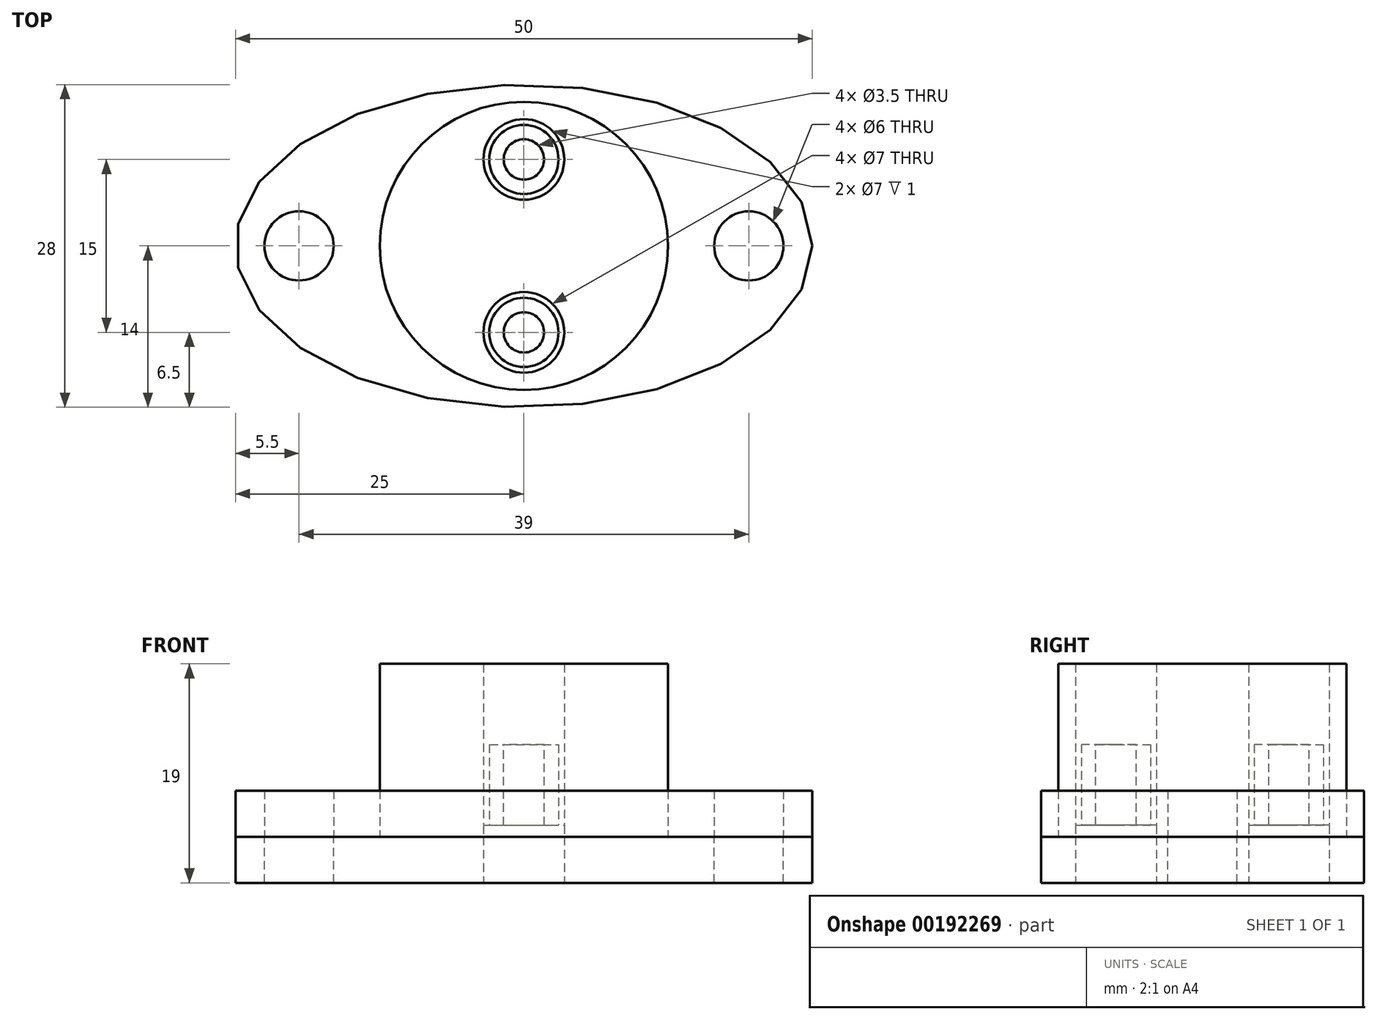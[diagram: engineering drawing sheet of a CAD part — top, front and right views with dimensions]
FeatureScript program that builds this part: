
annotation { "Feature Type Name" : "Feature", "Feature Type Description" : "" }
export const myFeature = defineFeature(function(context is Context, id is Id, definition is map)
    precondition{}
    {
        {
            var Q0;
            Q0=qCreatedBy(makeId("Top.planeOp"),FACE);
            var sketch = newSketch(context, id + "F0", { "sketchPlane" : qUnion([Q0])});
            skCircle(sketch, "E0", {"center": v(0, 0) * mm, "radius": 12.5 * mm});
            skCircle(sketch, "E1", {"center": v(0, 7.5) * mm, "radius": 3 * mm});
            skCircle(sketch, "E2", {"center": v(0, -7.5) * mm, "radius": 3 * mm});
            skCircle(sketch, "E3", {"center": v(0, -7.5) * mm, "radius": 3.5 * mm});
            skCircle(sketch, "E4", {"center": v(0, 7.5) * mm, "radius": 3.5 * mm});
            skSolve(sketch);
        }
        {
            var Q0;
            Q0=makeQuery(id+"F0.imprint","IMPRINT",FACE,{"disambiguationData":[TD([[makeQuery(id+"F0.imprint","IMPRINT",EDGE,{"derivedFrom":sQuery(id+"F0.wireOp",EDGE,"E1")}),1.0]])]});
            var Q1;
            Q1=makeQuery(id+"F0.imprint","IMPRINT",FACE,{"disambiguationData":[TD([[makeQuery(id+"F0.imprint","IMPRINT",EDGE,{"derivedFrom":sQuery(id+"F0.wireOp",EDGE,"E2")}),1.0]])]});
            extrude(context, id + "F1", {"entities" : qUnion([Q0, Q1]), "depth" : 8 * mm});
        }
        {
            var Q0;
            Q0=makeQuery(id+"F0.imprint","IMPRINT",FACE,{"disambiguationData":[TD([[makeQuery(id+"F0.imprint","IMPRINT",EDGE,{"derivedFrom":sQuery(id+"F0.wireOp",EDGE,"E0")}),1.0]])]});
            extrude(context, id + "F2", {"entities" : qUnion([Q0]), "depth" : 15 * mm});
        }
        {
            var Q0;
            Q0=makeQuery(id+"F2.opExtrude","CAP_FACE",FACE,{"disambiguationData":[OSD([sQuery(id+"F0.wireOp",EDGE,"E0"),sQuery(id+"F0.wireOp",EDGE,"E1"),sQuery(id+"F0.wireOp",EDGE,"E2")])],"isStart":true});
            var sketch = newSketch(context, id + "F3", { "sketchPlane" : qUnion([Q0])});
            skLineSegment(sketch, "E5", {"start": v(0, 0) * mm, "end": v(0, 14) * mm});
            skLineSegment(sketch, "E6", {"start": v(0, 0) * mm, "end": v(-25, 0) * mm});
            skLineSegment(sketch, "E7", {"start": v(0, 0) * mm, "end": v(25, 0) * mm});
            skLineSegment(sketch, "E8", {"start": v(0, 0) * mm, "end": v(0, -14) * mm});
            skEllipse(sketch, "E9", {"center": v(0, 0) * mm, "majorRadius": 25 * mm, "minorRadius": 14 * mm, "majorAxis": v(1, 0)});
            skSolve(sketch);
        }
        {
            var Q0;
            Q0 = qSketchRegion(id + "F3", true);
            extrude(context, id + "F4", {"entities" : qUnion([Q0]), "oppositeDirection" : true, "depth" : 4 * mm});
        }
        {
            var Q0;
            Q0=makeQuery(id+"F4.opExtrude","CAP_FACE",FACE,{"disambiguationData":[OSD([sQuery(id+"F3.wireOp",EDGE,"E9")])],"isStart":true});
            var sketch = newSketch(context, id + "F5", { "sketchPlane" : qUnion([Q0])});
            skCircle(sketch, "E10", {"center": v(-19.5, 0) * mm, "radius": 3 * mm});
            skCircle(sketch, "E11", {"center": v(19.5, 0) * mm, "radius": 3 * mm});
            skSolve(sketch);
        }
        {
            var Q0;
            Q0=makeQuery(id+"F5.imprint","IMPRINT",FACE,{"disambiguationData":[TD([[makeQuery(id+"F5.imprint","IMPRINT",EDGE,{"derivedFrom":sQuery(id+"F5.wireOp",EDGE,"E10")}),1.0]])]});
            var Q1;
            Q1=makeQuery(id+"F5.imprint","IMPRINT",FACE,{"disambiguationData":[TD([[makeQuery(id+"F5.imprint","IMPRINT",EDGE,{"derivedFrom":sQuery(id+"F5.wireOp",EDGE,"E11")}),1.0]])]});
            extrude(context, id + "F6", {"entities" : qUnion([Q0, Q1]), "operationType" : NewBodyOperationType.REMOVE, "oppositeDirection" : true, "depth" : 10 * mm});
        }
        {
            var Q0;
            Q0=makeQuery(id+"F4.opExtrude","CAP_FACE",FACE,{"disambiguationData":[OSD([sQuery(id+"F3.wireOp",EDGE,"E9")])],"isStart":true});
            var sketch = newSketch(context, id + "F7", { "sketchPlane" : qUnion([Q0])});
            skCircle(sketch, "E12", {"center": v(0, 7.5) * mm, "radius": 1.75 * mm});
            skCircle(sketch, "E13", {"center": v(0, -7.5) * mm, "radius": 1.75 * mm});
            skSolve(sketch);
        }
        {
            var Q0;
            Q0=makeQuery(id+"F1.opExtrude","CAP_FACE",FACE,{"disambiguationData":[OSD([sQuery(id+"F0.wireOp",EDGE,"E1")])],"isStart":false});
            var sketch = newSketch(context, id + "F8", { "sketchPlane" : qUnion([Q0])});
            skCircle(sketch, "E14", {"center": v(0, 7.5) * mm, "radius": 1.75 * mm});
            skSolve(sketch);
        }
        {
            var Q0;
            Q0 = qSketchRegion(id + "F8", true);
            extrude(context, id + "F9", {"entities" : qUnion([Q0]), "operationType" : NewBodyOperationType.REMOVE, "oppositeDirection" : true, "depth" : 10 * mm});
        }
        {
            var Q0;
            Q0=makeQuery(id+"F1.opExtrude","CAP_FACE",FACE,{"disambiguationData":[OSD([sQuery(id+"F0.wireOp",EDGE,"E2")])],"isStart":false});
            var sketch = newSketch(context, id + "F10", { "sketchPlane" : qUnion([Q0])});
            skCircle(sketch, "E15", {"center": v(0, -7.5) * mm, "radius": 1.75 * mm});
            skSolve(sketch);
        }
        {
            var Q0;
            Q0 = qSketchRegion(id + "F10", true);
            extrude(context, id + "F11", {"entities" : qUnion([Q0]), "operationType" : NewBodyOperationType.REMOVE, "oppositeDirection" : true, "depth" : 10 * mm});
        }
        {
            var Q0;
            Q0=makeQuery(id+"F7.imprint","IMPRINT",FACE,{"disambiguationData":[TD([[makeQuery(id+"F7.imprint","IMPRINT",EDGE,{"derivedFrom":sQuery(id+"F7.wireOp",EDGE,"E13")}),1.0]])]});
            var sketch = newSketch(context, id + "F12", { "sketchPlane" : qUnion([Q0])});
            skCircle(sketch, "E16", {"center": v(0, -7.5) * mm, "radius": 1.75 * mm});
            skSolve(sketch);
        }
        {
            var Q0;
            Q0 = qSketchRegion(id + "F12", true);
            extrude(context, id + "F13", {"entities" : qUnion([Q0]), "operationType" : NewBodyOperationType.REMOVE, "oppositeDirection" : true, "depth" : 10 * mm});
        }
        {
            var Q0;
            Q0=makeQuery(id+"F7.imprint","IMPRINT",FACE,{"disambiguationData":[TD([[makeQuery(id+"F7.imprint","IMPRINT",EDGE,{"derivedFrom":sQuery(id+"F7.wireOp",EDGE,"E12")}),1.0]])]});
            var sketch = newSketch(context, id + "F14", { "sketchPlane" : qUnion([Q0])});
            skCircle(sketch, "E17", {"center": v(0, 7.5) * mm, "radius": 1.75 * mm});
            skSolve(sketch);
        }
        {
            var Q0;
            Q0 = qSketchRegion(id + "F14", true);
            extrude(context, id + "F15", {"entities" : qUnion([Q0]), "operationType" : NewBodyOperationType.REMOVE, "oppositeDirection" : true, "depth" : 10 * mm});
        }
        {
            var Q0;
            Q0=makeQuery(id+"F7.imprint","IMPRINT",FACE,{"disambiguationData":[TD([[makeQuery(id+"F7.imprint","IMPRINT",EDGE,{"derivedFrom":sQuery(id+"F7.wireOp",EDGE,"E12")}),-1.0]])]});
            var sketch = newSketch(context, id + "F16", { "sketchPlane" : qUnion([Q0])});
            skSolve(sketch);
        }
        {
            var Q0;
            Q0 = qSketchRegion(id + "F16", true);
            var Q1;
            Q1=makeQuery(id+"F7.imprint","IMPRINT",FACE,{"disambiguationData":[TD([[makeQuery(id+"F7.imprint","IMPRINT",EDGE,{"derivedFrom":sQuery(id+"F7.wireOp",EDGE,"E12")}),-1.0]])]});
            extrude(context, id + "F17", {"entities" : qUnion([Q0, Q1]), "depth" : 4 * mm});
        }
        {
            var Q0;
            Q0=makeQuery(id+"F17.opExtrude","CAP_FACE",FACE,{"disambiguationData":[OSD([sQuery(id+"F3.wireOp",EDGE,"E9"),sQuery(id+"F5.wireOp",EDGE,"E10"),sQuery(id+"F5.wireOp",EDGE,"E11"),sQuery(id+"F7.wireOp",EDGE,"E12"),sQuery(id+"F7.wireOp",EDGE,"E13")])],"isStart":false});
            var sketch = newSketch(context, id + "F18", { "sketchPlane" : qUnion([Q0])});
            skLineSegment(sketch, "E18", {"start": v(0, 0) * mm, "end": v(0, 7.5) * mm});
            skCircle(sketch, "E19", {"center": v(0, 7.5) * mm, "radius": 3.5 * mm});
            skLineSegment(sketch, "E20", {"start": v(0, 0) * mm, "end": v(0, -7.5) * mm});
            skCircle(sketch, "E21", {"center": v(0, -7.5) * mm, "radius": 3.5 * mm});
            skSolve(sketch);
        }
        {
            var Q0;
            Q0 = qSketchRegion(id + "F18", true);
            extrude(context, id + "F19", {"entities" : qUnion([Q0]), "operationType" : NewBodyOperationType.REMOVE, "oppositeDirection" : true, "depth" : 5 * mm});
        }
    });
